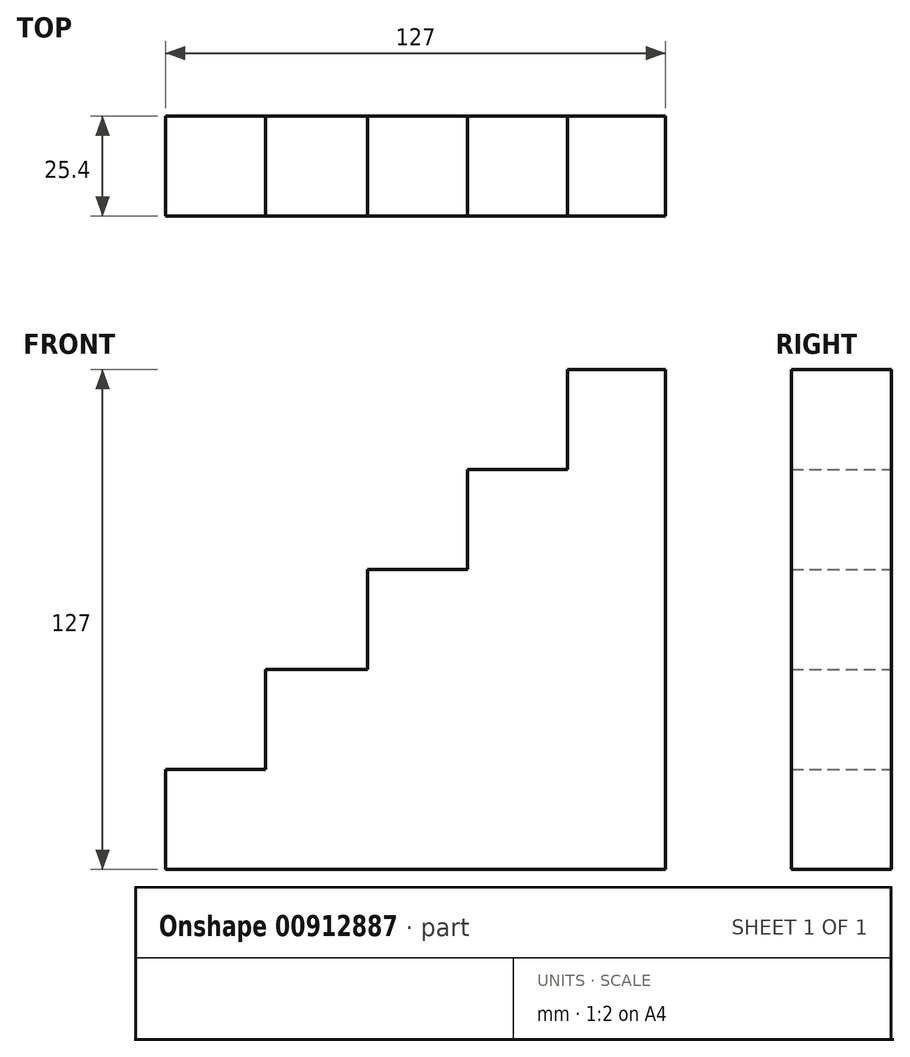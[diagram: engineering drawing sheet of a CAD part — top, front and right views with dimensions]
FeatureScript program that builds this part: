
annotation { "Feature Type Name" : "Feature", "Feature Type Description" : "" }
export const myFeature = defineFeature(function(context is Context, id is Id, definition is map)
    precondition{}
    {
        {
            var Q0;
            Q0=qCreatedBy(makeId("Front.planeOp"),FACE);
            var sketch = newSketch(context, id + "F0", { "sketchPlane" : qUnion([Q0])});
            skLineSegment(sketch, "E0", {"start": v(70.43, 72.33) * mm, "end": v(70.43, -52.46) * mm});
            skLineSegment(sketch, "E1", {"start": v(-56.57, -47.23) * mm, "end": v(70.43, -47.23) * mm});
            skLineSegment(sketch, "E2", {"start": v(-56.57, -47.23) * mm, "end": v(-56.57, -21.83) * mm});
            skLineSegment(sketch, "E3", {"start": v(-56.57, -21.83) * mm, "end": v(-31.17, -21.83) * mm});
            skLineSegment(sketch, "E4", {"start": v(-31.17, -21.83) * mm, "end": v(-31.17, 3.57) * mm});
            skLineSegment(sketch, "E5", {"start": v(-31.17, 3.57) * mm, "end": v(-5.27, 3.57) * mm});
            skLineSegment(sketch, "E6", {"start": v(-5.27, 3.57) * mm, "end": v(-5.27, 28.97) * mm});
            skLineSegment(sketch, "E7", {"start": v(-5.27, 28.97) * mm, "end": v(20.13, 28.97) * mm});
            skLineSegment(sketch, "E8", {"start": v(20.13, 28.97) * mm, "end": v(20.13, 54.37) * mm});
            skLineSegment(sketch, "E9", {"start": v(20.13, 54.37) * mm, "end": v(45.53, 54.37) * mm});
            skLineSegment(sketch, "E10", {"start": v(45.53, 54.37) * mm, "end": v(45.53, 79.77) * mm});
            skLineSegment(sketch, "E11", {"start": v(45.53, 79.77) * mm, "end": v(70.43, 79.77) * mm});
            skLineSegment(sketch, "E12", {"start": v(70.43, 79.77) * mm, "end": v(70.43, -47.23) * mm});
            skPoint(sketch, "E13.start.orphan", {"position": v(118.1, -21.83) * mm});
            skSolve(sketch);
        }
        {
            var Q0;
            Q0 = qSketchRegion(id + "F0", true);
            extrude(context, id + "F1", {"entities" : qUnion([Q0]), "depth" : 25.4 * mm, "offsetDistance" : 25.4 * mm});
        }
    });
